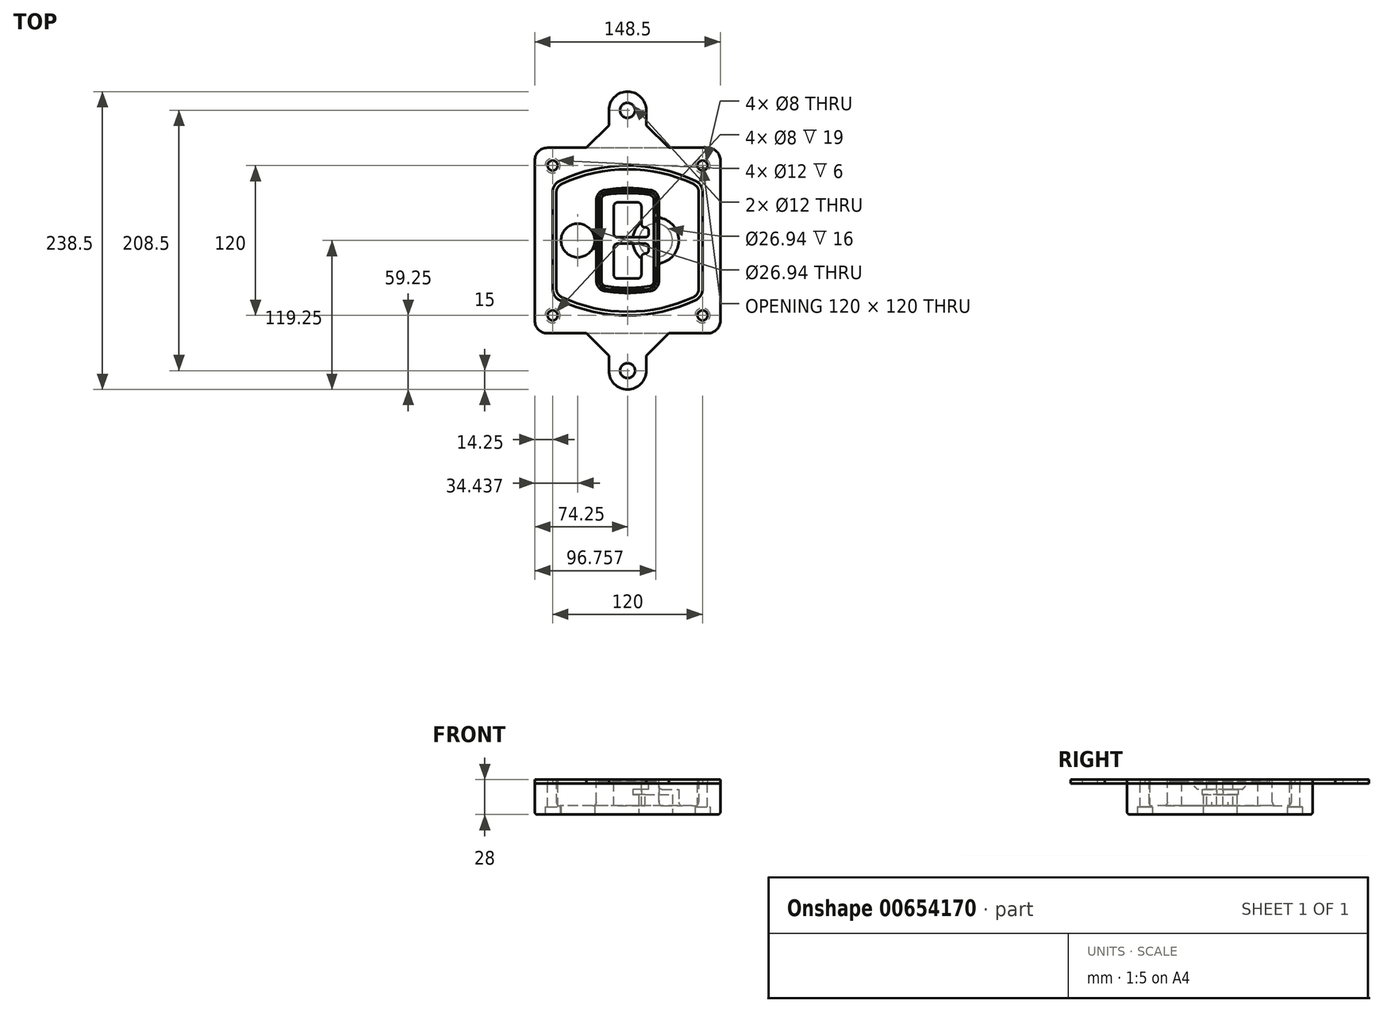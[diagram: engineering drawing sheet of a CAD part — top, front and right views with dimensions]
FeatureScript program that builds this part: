
annotation { "Feature Type Name" : "Feature", "Feature Type Description" : "" }
export const myFeature = defineFeature(function(context is Context, id is Id, definition is map)
    precondition{}
    {
        {
            var Q0;
            Q0=qCreatedBy(makeId("Top.planeOp"),FACE);
            var sketch = newSketch(context, id + "F0", { "sketchPlane" : qUnion([Q0])});
            skPoint(sketch, "E0.rect.middle", {"position": v(0, 0) * mm});
            skLineSegment(sketch, "E1.bottom", {"start": v(-64.25, -74.25) * mm, "end": v(64.25, -74.25) * mm});
            skLineSegment(sketch, "E1.top", {"start": v(-64.25, 74.25) * mm, "end": v(64.25, 74.25) * mm});
            skLineSegment(sketch, "E1.left", {"start": v(-74.25, -64.25) * mm, "end": v(-74.25, 64.25) * mm});
            skLineSegment(sketch, "E1.right", {"start": v(74.25, -64.25) * mm, "end": v(74.25, 64.25) * mm});
            skLineSegment(sketch, "E2", {"start": v(-74.25, 74.25) * mm, "end": v(74.25, -74.25) * mm, "construction": true});
            skLineSegment(sketch, "E3", {"start": v(74.25, 74.25) * mm, "end": v(-74.25, -74.25) * mm, "construction": true});
            skCircle(sketch, "E4", {"center": v(-60, 60) * mm, "radius": 4 * mm});
            skCircle(sketch, "E5", {"center": v(60, 60) * mm, "radius": 4 * mm});
            skCircle(sketch, "E6", {"center": v(60, -60) * mm, "radius": 4 * mm});
            skCircle(sketch, "E7", {"center": v(-60, -60) * mm, "radius": 4 * mm});
            skLineSegment(sketch, "E8", {"start": v(-60, 60) * mm, "end": v(60, 60) * mm, "construction": true});
            skLineSegment(sketch, "E9", {"start": v(60, 60) * mm, "end": v(60, -60) * mm, "construction": true});
            skLineSegment(sketch, "E10", {"start": v(60, -60) * mm, "end": v(-60, -60) * mm, "construction": true});
            skLineSegment(sketch, "E11", {"start": v(-60, -60) * mm, "end": v(-60, 60) * mm, "construction": true});
            skLineSegment(sketch, "E12", {"start": v(-60, 38.83) * mm, "end": v(-60, -38.83) * mm});
            skLineSegment(sketch, "E13", {"start": v(60, 38.83) * mm, "end": v(60, -38.83) * mm});
            skArc(sketch, "E14", {"start": v(54.26, 47.88) * mm, "mid": v(0, 60) * mm, "end": v(-54.26, 47.88) * mm});
            skArc(sketch, "E15", {"start": v(-54.26, -47.88) * mm, "mid": v(0, -60) * mm, "end": v(54.26, -47.88) * mm});
            skLineSegment(sketch, "E16", {"start": v(-60, 0) * mm, "end": v(60, 0) * mm, "construction": true});
            skPoint(sketch, "E17.visualSharp", {"position": v(-60, -45) * mm});
            skArc(sketch, "E17.filletArc", {"start": v(-60, -38.83) * mm, "mid": v(-58.44, -44.2) * mm, "end": v(-54.26, -47.88) * mm});
            skPoint(sketch, "E18.visualSharp", {"position": v(-60, 45) * mm});
            skArc(sketch, "E18.filletArc", {"start": v(-54.26, 47.88) * mm, "mid": v(-58.44, 44.2) * mm, "end": v(-60, 38.83) * mm});
            skPoint(sketch, "E19.visualSharp", {"position": v(60, 45) * mm});
            skArc(sketch, "E19.filletArc", {"start": v(60, 38.83) * mm, "mid": v(58.44, 44.2) * mm, "end": v(54.26, 47.88) * mm});
            skPoint(sketch, "E20.visualSharp", {"position": v(60, -45) * mm});
            skArc(sketch, "E20.filletArc", {"start": v(54.26, -47.88) * mm, "mid": v(58.44, -44.2) * mm, "end": v(60, -38.83) * mm});
            skPoint(sketch, "E21.visualSharp", {"position": v(-74.25, 74.25) * mm});
            skArc(sketch, "E21.filletArc", {"start": v(-64.25, 74.25) * mm, "mid": v(-71.32, 71.32) * mm, "end": v(-74.25, 64.25) * mm});
            skPoint(sketch, "E22.visualSharp", {"position": v(74.25, 74.25) * mm});
            skArc(sketch, "E22.filletArc", {"start": v(74.25, 64.25) * mm, "mid": v(71.32, 71.32) * mm, "end": v(64.25, 74.25) * mm});
            skPoint(sketch, "E23.visualSharp", {"position": v(74.25, -74.25) * mm});
            skArc(sketch, "E23.filletArc", {"start": v(64.25, -74.25) * mm, "mid": v(71.32, -71.32) * mm, "end": v(74.25, -64.25) * mm});
            skPoint(sketch, "E24.visualSharp", {"position": v(-74.25, -74.25) * mm});
            skArc(sketch, "E24.filletArc", {"start": v(-74.25, -64.25) * mm, "mid": v(-71.32, -71.32) * mm, "end": v(-64.25, -74.25) * mm});
            skArc(sketch, "E25.0", {"start": v(57, 38.83) * mm, "mid": v(55.9, 42.58) * mm, "end": v(52.98, 45.17) * mm});
            skLineSegment(sketch, "E25.1", {"start": v(57, 38.83) * mm, "end": v(57, -38.83) * mm});
            skArc(sketch, "E25.2", {"start": v(52.98, -45.17) * mm, "mid": v(55.9, -42.58) * mm, "end": v(57, -38.83) * mm});
            skArc(sketch, "E25.3", {"start": v(-52.98, -45.17) * mm, "mid": v(0, -57) * mm, "end": v(52.98, -45.17) * mm});
            skArc(sketch, "E25.4", {"start": v(-57, -38.83) * mm, "mid": v(-55.9, -42.58) * mm, "end": v(-52.98, -45.17) * mm});
            skArc(sketch, "E25.5", {"start": v(52.98, 45.17) * mm, "mid": v(0, 57) * mm, "end": v(-52.98, 45.17) * mm});
            skLineSegment(sketch, "E25.6", {"start": v(-57, 38.83) * mm, "end": v(-57, -38.83) * mm});
            skArc(sketch, "E25.7", {"start": v(-52.98, 45.17) * mm, "mid": v(-55.9, 42.58) * mm, "end": v(-57, 38.83) * mm});
            skArc(sketch, "E26.0", {"start": v(-55.96, 51.5) * mm, "mid": v(-61.82, 46.33) * mm, "end": v(-64, 38.83) * mm});
            skArc(sketch, "E26.1", {"start": v(55.96, 51.5) * mm, "mid": v(0, 64) * mm, "end": v(-55.96, 51.5) * mm});
            skArc(sketch, "E26.2", {"start": v(64, 38.83) * mm, "mid": v(61.82, 46.33) * mm, "end": v(55.96, 51.5) * mm});
            skLineSegment(sketch, "E26.3", {"start": v(64, 38.83) * mm, "end": v(64, -38.83) * mm});
            skArc(sketch, "E26.4", {"start": v(55.96, -51.5) * mm, "mid": v(61.82, -46.33) * mm, "end": v(64, -38.83) * mm});
            skLineSegment(sketch, "E26.5", {"start": v(-64, 38.83) * mm, "end": v(-64, -38.83) * mm});
            skArc(sketch, "E26.6", {"start": v(-55.96, -51.5) * mm, "mid": v(0, -64) * mm, "end": v(55.96, -51.5) * mm});
            skArc(sketch, "E26.7", {"start": v(-64, -38.83) * mm, "mid": v(-61.82, -46.33) * mm, "end": v(-55.96, -51.5) * mm});
            skLineSegment(sketch, "E27", {"start": v(0, 74.25) * mm, "end": v(0, 104.25) * mm, "construction": true});
            skCircle(sketch, "E28", {"center": v(0, 104.25) * mm, "radius": 6 * mm});
            skArc(sketch, "E29", {"start": v(-15, 104.25) * mm, "mid": v(0, 119.25) * mm, "end": v(15, 104.25) * mm});
            skLineSegment(sketch, "E30", {"start": v(-15, 104.25) * mm, "end": v(-15, 92.25) * mm});
            skLineSegment(sketch, "E31", {"start": v(15, 104.25) * mm, "end": v(15, 92.25) * mm});
            skLineSegment(sketch, "E32", {"start": v(-15, 92.25) * mm, "end": v(-33, 74.25) * mm});
            skLineSegment(sketch, "E33", {"start": v(15, 92.25) * mm, "end": v(33, 74.25) * mm});
            skLineSegment(sketch, "E34", {"start": v(0, -74.25) * mm, "end": v(0, -104.25) * mm, "construction": true});
            skCircle(sketch, "E35", {"center": v(0, -104.25) * mm, "radius": 6 * mm});
            skArc(sketch, "E36", {"start": v(15, -104.25) * mm, "mid": v(0, -119.25) * mm, "end": v(-15, -104.25) * mm});
            skLineSegment(sketch, "E37", {"start": v(15, -104.25) * mm, "end": v(15, -92.25) * mm});
            skLineSegment(sketch, "E38", {"start": v(-15, -104.25) * mm, "end": v(-15, -92.25) * mm});
            skLineSegment(sketch, "E39", {"start": v(15, -92.25) * mm, "end": v(33, -74.25) * mm});
            skLineSegment(sketch, "E40", {"start": v(-15, -92.25) * mm, "end": v(-33, -74.25) * mm});
            skSolve(sketch);
        }
        {
            var Q0;
            Q0=makeQuery(id+"F0.imprint","IMPRINT",FACE,{"disambiguationData":[TD([[makeQuery(id+"F0.imprint","IMPRINT",EDGE,{"derivedFrom":sQuery(id+"F0.wireOp",EDGE,"E1.bottom")}),1.0]])]});
            var Q1;
            Q1=makeQuery(id+"F0.imprint","IMPRINT",FACE,{"disambiguationData":[TD([[makeQuery(id+"F0.imprint","IMPRINT",EDGE,{"derivedFrom":sQuery(id+"F0.wireOp",EDGE,"E12")}),1.0]])]});
            var Q2;
            Q2=makeQuery(id+"F0.imprint","IMPRINT",FACE,{"disambiguationData":[TD([[makeQuery(id+"F0.imprint","IMPRINT",EDGE,{"derivedFrom":sQuery(id+"F0.wireOp",EDGE,"E25.0")}),1.0]])]});
            var Q3;
            Q3=makeQuery(id+"F0.imprint","IMPRINT",FACE,{"disambiguationData":[TD([[makeQuery(id+"F0.imprint","IMPRINT",EDGE,{"derivedFrom":sQuery(id+"F0.wireOp",EDGE,"E12")}),-1.0]])]});
            extrude(context, id + "F1", {"entities" : qUnion([Q0, Q1, Q2, Q3]), "oppositeDirection" : true, "depth" : 25 * mm});
        }
        {
            var Q0;
            Q0=makeQuery(id+"F0.imprint","IMPRINT",FACE,{"disambiguationData":[TD([[makeQuery(id+"F0.imprint","IMPRINT",EDGE,{"derivedFrom":sQuery(id+"F0.wireOp",EDGE,"E12")}),1.0]])]});
            extrude(context, id + "F2", {"entities" : qUnion([Q0]), "operationType" : NewBodyOperationType.ADD, "depth" : 3 * mm});
        }
        {
            var Q0;
            Q0=makeQuery(id+"F0.imprint","IMPRINT",FACE,{"disambiguationData":[TD([[makeQuery(id+"F0.imprint","IMPRINT",EDGE,{"derivedFrom":sQuery(id+"F0.wireOp",EDGE,"E25.0")}),1.0]])]});
            extrude(context, id + "F3", {"entities" : qUnion([Q0]), "operationType" : NewBodyOperationType.REMOVE, "oppositeDirection" : true, "depth" : 18 * mm});
        }
        {
            var Q0;
            Q0=makeQuery(id+"F2.opExtrude","CAP_FACE",FACE,{"disambiguationData":[OSD([sQuery(id+"F0.wireOp",EDGE,"E12"),sQuery(id+"F0.wireOp",EDGE,"E13"),sQuery(id+"F0.wireOp",EDGE,"E14"),sQuery(id+"F0.wireOp",EDGE,"E15"),sQuery(id+"F0.wireOp",EDGE,"E17.filletArc"),sQuery(id+"F0.wireOp",EDGE,"E18.filletArc"),sQuery(id+"F0.wireOp",EDGE,"E19.filletArc"),sQuery(id+"F0.wireOp",EDGE,"E20.filletArc"),sQuery(id+"F0.wireOp",EDGE,"E25.0"),sQuery(id+"F0.wireOp",EDGE,"E25.1"),sQuery(id+"F0.wireOp",EDGE,"E25.2"),sQuery(id+"F0.wireOp",EDGE,"E25.3"),sQuery(id+"F0.wireOp",EDGE,"E25.4"),sQuery(id+"F0.wireOp",EDGE,"E25.5"),sQuery(id+"F0.wireOp",EDGE,"E25.6"),sQuery(id+"F0.wireOp",EDGE,"E25.7")])],"isStart":false});
            var sketch = newSketch(context, id + "F4", { "sketchPlane" : qUnion([Q0])});
            skArc(sketch, "E41.0", {"start": v(-18.34, -40.45) * mm, "mid": v(0, -42) * mm, "end": v(18.34, -40.45) * mm});
            skArc(sketch, "E42.0", {"start": v(18.34, 40.45) * mm, "mid": v(0, 42) * mm, "end": v(-18.34, 40.45) * mm});
            skLineSegment(sketch, "E43", {"start": v(-25, 32.57) * mm, "end": v(-25, -32.57) * mm});
            skLineSegment(sketch, "E44", {"start": v(25, 32.57) * mm, "end": v(25, -32.57) * mm});
            skLineSegment(sketch, "E45", {"start": v(-25, 39.1) * mm, "end": v(25, 39.1) * mm, "construction": true});
            skLineSegment(sketch, "E46", {"start": v(-25, -39.1) * mm, "end": v(25, -39.1) * mm, "construction": true});
            skPoint(sketch, "E47.visualSharp", {"position": v(-25, 39.1) * mm});
            skArc(sketch, "E47.filletArc", {"start": v(-18.34, 40.45) * mm, "mid": v(-23.11, 37.73) * mm, "end": v(-25, 32.57) * mm});
            skPoint(sketch, "E48.visualSharp", {"position": v(25, 39.1) * mm});
            skArc(sketch, "E48.filletArc", {"start": v(25, 32.57) * mm, "mid": v(23.11, 37.73) * mm, "end": v(18.34, 40.45) * mm});
            skPoint(sketch, "E49.visualSharp", {"position": v(25, -39.1) * mm});
            skArc(sketch, "E49.filletArc", {"start": v(18.34, -40.45) * mm, "mid": v(23.11, -37.73) * mm, "end": v(25, -32.57) * mm});
            skPoint(sketch, "E50.visualSharp", {"position": v(-25, -39.1) * mm});
            skArc(sketch, "E50.filletArc", {"start": v(-25, -32.57) * mm, "mid": v(-23.11, -37.73) * mm, "end": v(-18.34, -40.45) * mm});
            skArc(sketch, "E51.0", {"start": v(52.98, 45.17) * mm, "mid": v(0, 57) * mm, "end": v(-52.98, 45.17) * mm});
            skArc(sketch, "E51.1", {"start": v(-52.98, 45.17) * mm, "mid": v(-55.9, 42.58) * mm, "end": v(-57, 38.83) * mm});
            skLineSegment(sketch, "E51.2", {"start": v(-57, 38.83) * mm, "end": v(-57, -38.83) * mm});
            skArc(sketch, "E51.3", {"start": v(-57, -38.83) * mm, "mid": v(-55.9, -42.58) * mm, "end": v(-52.98, -45.17) * mm});
            skArc(sketch, "E51.4", {"start": v(-52.98, -45.17) * mm, "mid": v(0, -57) * mm, "end": v(52.98, -45.17) * mm});
            skArc(sketch, "E51.5", {"start": v(52.98, -45.17) * mm, "mid": v(55.9, -42.58) * mm, "end": v(57, -38.83) * mm});
            skLineSegment(sketch, "E51.6", {"start": v(57, 38.83) * mm, "end": v(57, -38.83) * mm});
            skArc(sketch, "E51.7", {"start": v(57, 38.83) * mm, "mid": v(55.9, 42.58) * mm, "end": v(52.98, 45.17) * mm});
            skLineSegment(sketch, "E52.0", {"start": v(23, 32.57) * mm, "end": v(23, -32.57) * mm});
            skArc(sketch, "E52.1", {"start": v(18, -38.48) * mm, "mid": v(21.58, -36.44) * mm, "end": v(23, -32.57) * mm});
            skArc(sketch, "E52.2", {"start": v(-18, -38.48) * mm, "mid": v(0, -40) * mm, "end": v(18, -38.48) * mm});
            skArc(sketch, "E52.3", {"start": v(-23, -32.57) * mm, "mid": v(-21.58, -36.44) * mm, "end": v(-18, -38.48) * mm});
            skLineSegment(sketch, "E52.4", {"start": v(-23, 32.57) * mm, "end": v(-23, -32.57) * mm});
            skArc(sketch, "E52.5", {"start": v(23, 32.57) * mm, "mid": v(21.58, 36.44) * mm, "end": v(18, 38.48) * mm});
            skArc(sketch, "E52.6", {"start": v(-18, 38.48) * mm, "mid": v(-21.58, 36.44) * mm, "end": v(-23, 32.57) * mm});
            skArc(sketch, "E52.7", {"start": v(18, 38.48) * mm, "mid": v(0, 40) * mm, "end": v(-18, 38.48) * mm});
            skArc(sketch, "E53.0", {"start": v(21, 32.57) * mm, "mid": v(20.06, 35.15) * mm, "end": v(17.67, 36.5) * mm});
            skLineSegment(sketch, "E53.1", {"start": v(21, 32.57) * mm, "end": v(21, -32.57) * mm});
            skArc(sketch, "E53.2", {"start": v(17.67, -36.5) * mm, "mid": v(20.06, -35.15) * mm, "end": v(21, -32.57) * mm});
            skArc(sketch, "E53.3", {"start": v(-17.67, -36.5) * mm, "mid": v(0, -38) * mm, "end": v(17.67, -36.5) * mm});
            skArc(sketch, "E53.4", {"start": v(-21, -32.57) * mm, "mid": v(-20.06, -35.15) * mm, "end": v(-17.67, -36.5) * mm});
            skArc(sketch, "E53.5", {"start": v(17.67, 36.5) * mm, "mid": v(0, 38) * mm, "end": v(-17.67, 36.5) * mm});
            skLineSegment(sketch, "E53.6", {"start": v(-21, 32.57) * mm, "end": v(-21, -32.57) * mm});
            skArc(sketch, "E53.7", {"start": v(-17.67, 36.5) * mm, "mid": v(-20.06, 35.15) * mm, "end": v(-21, 32.57) * mm});
            skLineSegment(sketch, "E54", {"start": v(-25, 0) * mm, "end": v(25, 0) * mm, "construction": true});
            skLineSegment(sketch, "E55", {"start": v(-11, 5.5) * mm, "end": v(-11, 27.5) * mm});
            skLineSegment(sketch, "E56", {"start": v(-8, 30.5) * mm, "end": v(8, 30.5) * mm});
            skLineSegment(sketch, "E57", {"start": v(11, 27.5) * mm, "end": v(11, 13.5) * mm});
            skLineSegment(sketch, "E58", {"start": v(14, 10.5) * mm, "end": v(14, 10.5) * mm});
            skLineSegment(sketch, "E59", {"start": v(17, 7.5) * mm, "end": v(17, 5.5) * mm});
            skLineSegment(sketch, "E60", {"start": v(14, 2.5) * mm, "end": v(-8, 2.5) * mm});
            skPoint(sketch, "E61.visualSharp", {"position": v(-11, 30.5) * mm});
            skArc(sketch, "E61.filletArc", {"start": v(-8, 30.5) * mm, "mid": v(-10.12, 29.62) * mm, "end": v(-11, 27.5) * mm});
            skPoint(sketch, "E62.visualSharp", {"position": v(11, 30.5) * mm});
            skArc(sketch, "E62.filletArc", {"start": v(11, 27.5) * mm, "mid": v(10.12, 29.62) * mm, "end": v(8, 30.5) * mm});
            skPoint(sketch, "E63.visualSharp", {"position": v(11, 10.5) * mm});
            skArc(sketch, "E63.filletArc", {"start": v(11, 13.5) * mm, "mid": v(11.88, 11.38) * mm, "end": v(14, 10.5) * mm});
            skPoint(sketch, "E64.visualSharp", {"position": v(17, 10.5) * mm});
            skArc(sketch, "E64.filletArc", {"start": v(17, 7.5) * mm, "mid": v(16.12, 9.62) * mm, "end": v(14, 10.5) * mm});
            skPoint(sketch, "E65.visualSharp", {"position": v(17, 2.5) * mm});
            skArc(sketch, "E65.filletArc", {"start": v(14, 2.5) * mm, "mid": v(16.12, 3.38) * mm, "end": v(17, 5.5) * mm});
            skPoint(sketch, "E66.visualSharp", {"position": v(-11, 2.5) * mm});
            skArc(sketch, "E66.filletArc", {"start": v(-11, 5.5) * mm, "mid": v(-10.12, 3.38) * mm, "end": v(-8, 2.5) * mm});
            skLineSegment(sketch, "E67.0.MirrorCS", {"start": v(14, -2.5) * mm, "end": v(-8, -2.5) * mm});
            skArc(sketch, "E68.0.MirrorCS", {"start": v(-11, -5.5) * mm, "mid": v(-10.12, -3.38) * mm, "end": v(-8, -2.5) * mm});
            skLineSegment(sketch, "E69.0.MirrorCS", {"start": v(-11, -5.5) * mm, "end": v(-11, -27.5) * mm});
            skArc(sketch, "E70.0.MirrorCS", {"start": v(-8, -30.5) * mm, "mid": v(-10.12, -29.62) * mm, "end": v(-11, -27.5) * mm});
            skLineSegment(sketch, "E71.0.MirrorCS", {"start": v(-8, -30.5) * mm, "end": v(8, -30.5) * mm});
            skArc(sketch, "E72.0.MirrorCS", {"start": v(11, -27.5) * mm, "mid": v(10.12, -29.62) * mm, "end": v(8, -30.5) * mm});
            skLineSegment(sketch, "E73.0.MirrorCS", {"start": v(11, -27.5) * mm, "end": v(11, -13.5) * mm});
            skArc(sketch, "E74.0.MirrorCS", {"start": v(11, -13.5) * mm, "mid": v(11.88, -11.38) * mm, "end": v(14, -10.5) * mm});
            skArc(sketch, "E75.0.MirrorCS", {"start": v(17, -7.5) * mm, "mid": v(16.12, -9.62) * mm, "end": v(14, -10.5) * mm});
            skLineSegment(sketch, "E76.0.MirrorCS", {"start": v(17, -7.5) * mm, "end": v(17, -5.5) * mm});
            skArc(sketch, "E77.0.MirrorCS", {"start": v(14, -2.5) * mm, "mid": v(16.12, -3.38) * mm, "end": v(17, -5.5) * mm});
            skSolve(sketch);
        }
        {
            var Q0;
            Q0=makeQuery(id+"F4.imprint","IMPRINT",FACE,{"disambiguationData":[TD([[makeQuery(id+"F4.imprint","IMPRINT",EDGE,{"derivedFrom":sQuery(id+"F4.wireOp",EDGE,"E41.0")}),1.0]])]});
            var Q1;
            Q1=makeQuery(id+"F4.imprint","IMPRINT",FACE,{"disambiguationData":[TD([[makeQuery(id+"F4.imprint","IMPRINT",EDGE,{"derivedFrom":sQuery(id+"F4.wireOp",EDGE,"E52.0")}),-1.0]])]});
            var Q2;
            Q2=makeQuery(id+"F4.imprint","IMPRINT",FACE,{"disambiguationData":[TD([[makeQuery(id+"F4.imprint","IMPRINT",EDGE,{"derivedFrom":sQuery(id+"F4.wireOp",EDGE,"E53.0")}),1.0]])]});
            extrude(context, id + "F5", {"entities" : qUnion([Q0, Q1, Q2]), "operationType" : NewBodyOperationType.ADD, "endBound" : BoundingType.UP_TO_NEXT, "oppositeDirection" : true, "depth" : 25 * mm});
        }
        {
            var Q0;
            Q0=makeQuery(id+"F4.imprint","IMPRINT",FACE,{"disambiguationData":[TD([[makeQuery(id+"F4.imprint","IMPRINT",EDGE,{"derivedFrom":sQuery(id+"F4.wireOp",EDGE,"E52.0")}),-1.0]])]});
            extrude(context, id + "F6", {"entities" : qUnion([Q0]), "operationType" : NewBodyOperationType.REMOVE, "oppositeDirection" : true, "depth" : 2 * mm});
        }
        {
            var Q0;
            Q0=makeQuery(id+"F1.opExtrude","CAP_FACE",FACE,{"disambiguationData":[OSD([sQuery(id+"F0.wireOp",EDGE,"E1.bottom"),sQuery(id+"F0.wireOp",EDGE,"E1.top"),sQuery(id+"F0.wireOp",EDGE,"E1.left"),sQuery(id+"F0.wireOp",EDGE,"E1.right"),sQuery(id+"F0.wireOp",EDGE,"E4"),sQuery(id+"F0.wireOp",EDGE,"E5"),sQuery(id+"F0.wireOp",EDGE,"E6"),sQuery(id+"F0.wireOp",EDGE,"E7"),sQuery(id+"F0.wireOp",EDGE,"E21.filletArc"),sQuery(id+"F0.wireOp",EDGE,"E22.filletArc"),sQuery(id+"F0.wireOp",EDGE,"E23.filletArc"),sQuery(id+"F0.wireOp",EDGE,"E24.filletArc")])],"isStart":false});
            var sketch = newSketch(context, id + "F7", { "sketchPlane" : qUnion([Q0])});
            skCircle(sketch, "E78", {"center": v(22.5, 0) * mm, "radius": 13.47 * mm});
            skCircle(sketch, "E79", {"center": v(-39.81, 0) * mm, "radius": 13.47 * mm});
            skLineSegment(sketch, "E80", {"start": v(74.25, 0) * mm, "end": v(-74.25, 0) * mm});
            skCircle(sketch, "E81", {"center": v(22.5, 0) * mm, "radius": 18.47 * mm});
            skCircle(sketch, "E82", {"center": v(60, -60) * mm, "radius": 6 * mm});
            skCircle(sketch, "E83", {"center": v(-60, -60) * mm, "radius": 6 * mm});
            skCircle(sketch, "E84", {"center": v(-60, 60) * mm, "radius": 6 * mm});
            skCircle(sketch, "E85", {"center": v(60, 60) * mm, "radius": 6 * mm});
            skSolve(sketch);
        }
        {
            var Q0;
            {var subQ1=sQuery(id+"F7.wireOp",EDGE,"E80");var subQ4=sQuery(id+"F7.wireOp",EDGE,"E78");var subQ6=makeQuery(id+"F7.imprint","INTERSECT",VERTEX,{"disambiguationData":[OD(0.0)],"derivedFrom":[subQ4,subQ1]});Q0=makeQuery(id+"F7.imprint","IMPRINT",FACE,{"disambiguationData":[TD([[makeQuery(id+"F7.imprint","IMPRINT",EDGE,{"disambiguationData":[TD([[subQ6,-1.0]])],"derivedFrom":subQ4}),-1.0]])]});}
            var Q1;
            {var subQ0=sQuery(id+"F7.wireOp",EDGE,"E80");var subQ1=sQuery(id+"F7.wireOp",EDGE,"E78");var subQ3=makeQuery(id+"F7.imprint","INTERSECT",VERTEX,{"disambiguationData":[OD(0.0)],"derivedFrom":[subQ1,subQ0]});Q1=makeQuery(id+"F7.imprint","IMPRINT",FACE,{"disambiguationData":[TD([[makeQuery(id+"F7.imprint","IMPRINT",EDGE,{"disambiguationData":[TD([[subQ3,-1.0]])],"derivedFrom":subQ1}),1.0]])]});}
            var Q2;
            {var subQ0=sQuery(id+"F7.wireOp",EDGE,"E80");var subQ1=sQuery(id+"F7.wireOp",EDGE,"E78");var subQ3=makeQuery(id+"F7.imprint","INTERSECT",VERTEX,{"disambiguationData":[OD(0.0)],"derivedFrom":[subQ1,subQ0]});Q2=makeQuery(id+"F7.imprint","IMPRINT",FACE,{"disambiguationData":[TD([[makeQuery(id+"F7.imprint","IMPRINT",EDGE,{"disambiguationData":[TD([[subQ3,1.0]])],"derivedFrom":subQ1}),1.0]])]});}
            var Q3;
            {var subQ1=sQuery(id+"F7.wireOp",EDGE,"E80");var subQ4=sQuery(id+"F7.wireOp",EDGE,"E78");var subQ6=makeQuery(id+"F7.imprint","INTERSECT",VERTEX,{"disambiguationData":[OD(0.0)],"derivedFrom":[subQ4,subQ1]});Q3=makeQuery(id+"F7.imprint","IMPRINT",FACE,{"disambiguationData":[TD([[makeQuery(id+"F7.imprint","IMPRINT",EDGE,{"disambiguationData":[TD([[subQ6,1.0]])],"derivedFrom":subQ4}),-1.0]])]});}
            extrude(context, id + "F8", {"entities" : qUnion([Q0, Q1, Q2, Q3]), "operationType" : NewBodyOperationType.ADD, "oppositeDirection" : true, "depth" : 20 * mm});
        }
        {
            var Q0;
            {var subQ0=sQuery(id+"F7.wireOp",EDGE,"E80");var subQ1=sQuery(id+"F7.wireOp",EDGE,"E78");var subQ3=makeQuery(id+"F7.imprint","INTERSECT",VERTEX,{"disambiguationData":[OD(0.0)],"derivedFrom":[subQ1,subQ0]});Q0=makeQuery(id+"F7.imprint","IMPRINT",FACE,{"disambiguationData":[TD([[makeQuery(id+"F7.imprint","IMPRINT",EDGE,{"disambiguationData":[TD([[subQ3,-1.0]])],"derivedFrom":subQ1}),1.0]])]});}
            var Q1;
            {var subQ0=sQuery(id+"F7.wireOp",EDGE,"E80");var subQ1=sQuery(id+"F7.wireOp",EDGE,"E78");var subQ3=makeQuery(id+"F7.imprint","INTERSECT",VERTEX,{"disambiguationData":[OD(0.0)],"derivedFrom":[subQ1,subQ0]});Q1=makeQuery(id+"F7.imprint","IMPRINT",FACE,{"disambiguationData":[TD([[makeQuery(id+"F7.imprint","IMPRINT",EDGE,{"disambiguationData":[TD([[subQ3,1.0]])],"derivedFrom":subQ1}),1.0]])]});}
            extrude(context, id + "F9", {"entities" : qUnion([Q0, Q1]), "operationType" : NewBodyOperationType.REMOVE, "oppositeDirection" : true, "depth" : 16 * mm});
        }
        {
            var Q0;
            {var subQ0=sQuery(id+"F7.wireOp",EDGE,"E80");var subQ1=sQuery(id+"F7.wireOp",EDGE,"E79");var subQ3=makeQuery(id+"F7.imprint","INTERSECT",VERTEX,{"disambiguationData":[OD(0.0)],"derivedFrom":[subQ1,subQ0]});Q0=makeQuery(id+"F7.imprint","IMPRINT",FACE,{"disambiguationData":[TD([[makeQuery(id+"F7.imprint","IMPRINT",EDGE,{"disambiguationData":[TD([[subQ3,-1.0]])],"derivedFrom":subQ1}),1.0]])]});}
            var Q1;
            {var subQ0=sQuery(id+"F7.wireOp",EDGE,"E80");var subQ1=sQuery(id+"F7.wireOp",EDGE,"E79");var subQ3=makeQuery(id+"F7.imprint","INTERSECT",VERTEX,{"disambiguationData":[OD(0.0)],"derivedFrom":[subQ1,subQ0]});Q1=makeQuery(id+"F7.imprint","IMPRINT",FACE,{"disambiguationData":[TD([[makeQuery(id+"F7.imprint","IMPRINT",EDGE,{"disambiguationData":[TD([[subQ3,1.0]])],"derivedFrom":subQ1}),1.0]])]});}
            extrude(context, id + "F10", {"entities" : qUnion([Q0, Q1]), "operationType" : NewBodyOperationType.REMOVE, "oppositeDirection" : true, "depth" : 25 * mm});
        }
        {
            var Q0;
            Q0=makeQuery(id+"F7.imprint","IMPRINT",FACE,{"disambiguationData":[TD([[makeQuery(id+"F7.imprint","IMPRINT",EDGE,{"derivedFrom":sQuery(id+"F7.wireOp",EDGE,"E82")}),1.0]])]});
            var Q1;
            Q1=makeQuery(id+"F7.imprint","IMPRINT",FACE,{"disambiguationData":[TD([[makeQuery(id+"F7.imprint","IMPRINT",EDGE,{"derivedFrom":makeQuery(id+"F1.opExtrude","CAP_EDGE",EDGE,{"disambiguationData":[OSD([sQuery(id+"F0.wireOp",EDGE,"E5")])],"isStart":false})}),-1.0]])]});
            var Q2;
            Q2=makeQuery(id+"F7.imprint","IMPRINT",FACE,{"disambiguationData":[TD([[makeQuery(id+"F7.imprint","IMPRINT",EDGE,{"derivedFrom":sQuery(id+"F7.wireOp",EDGE,"E83")}),1.0]])]});
            var Q3;
            Q3=makeQuery(id+"F7.imprint","IMPRINT",FACE,{"disambiguationData":[TD([[makeQuery(id+"F7.imprint","IMPRINT",EDGE,{"derivedFrom":makeQuery(id+"F1.opExtrude","CAP_EDGE",EDGE,{"disambiguationData":[OSD([sQuery(id+"F0.wireOp",EDGE,"E4")])],"isStart":false})}),-1.0]])]});
            var Q4;
            Q4=makeQuery(id+"F7.imprint","IMPRINT",FACE,{"disambiguationData":[TD([[makeQuery(id+"F7.imprint","IMPRINT",EDGE,{"derivedFrom":sQuery(id+"F7.wireOp",EDGE,"E84")}),1.0]])]});
            var Q5;
            Q5=makeQuery(id+"F7.imprint","IMPRINT",FACE,{"disambiguationData":[TD([[makeQuery(id+"F7.imprint","IMPRINT",EDGE,{"derivedFrom":makeQuery(id+"F1.opExtrude","CAP_EDGE",EDGE,{"disambiguationData":[OSD([sQuery(id+"F0.wireOp",EDGE,"E7")])],"isStart":false})}),-1.0]])]});
            var Q6;
            Q6=makeQuery(id+"F7.imprint","IMPRINT",FACE,{"disambiguationData":[TD([[makeQuery(id+"F7.imprint","IMPRINT",EDGE,{"derivedFrom":sQuery(id+"F7.wireOp",EDGE,"E85")}),1.0]])]});
            var Q7;
            Q7=makeQuery(id+"F7.imprint","IMPRINT",FACE,{"disambiguationData":[TD([[makeQuery(id+"F7.imprint","IMPRINT",EDGE,{"derivedFrom":makeQuery(id+"F1.opExtrude","CAP_EDGE",EDGE,{"disambiguationData":[OSD([sQuery(id+"F0.wireOp",EDGE,"E6")])],"isStart":false})}),-1.0]])]});
            extrude(context, id + "F11", {"entities" : qUnion([Q0, Q1, Q2, Q3, Q4, Q5, Q6, Q7]), "operationType" : NewBodyOperationType.REMOVE, "oppositeDirection" : true, "depth" : 6 * mm});
        }
        {
            var Q0;
            Q0=makeQuery(id+"F9.boolean.opBoolean","COPY",FACE,{"derivedFrom":makeQuery(id+"F9.opExtrude","CAP_FACE",FACE,{"disambiguationData":[OSD([sQuery(id+"F7.wireOp",EDGE,"E78")])],"isStart":false})});
            var sketch = newSketch(context, id + "F12", { "sketchPlane" : qUnion([Q0])});
            skArc(sketch, "E86.0", {"start": v(11, 14.45) * mm, "mid": v(6.45, 9.13) * mm, "end": v(4.2, 2.5) * mm});
            skArc(sketch, "E86.1", {"start": v(4.2, -2.5) * mm, "mid": v(6.45, -9.13) * mm, "end": v(11, -14.45) * mm});
            skLineSegment(sketch, "E87", {"start": v(4.2, -2.5) * mm, "end": v(14, -2.5) * mm});
            skLineSegment(sketch, "E88.0", {"start": v(14, 2.5) * mm, "end": v(4.2, 2.5) * mm});
            skArc(sketch, "E88.1", {"start": v(14, 2.5) * mm, "mid": v(16.12, 3.38) * mm, "end": v(17, 5.5) * mm});
            skLineSegment(sketch, "E88.2", {"start": v(17, 7.5) * mm, "end": v(17, 5.5) * mm});
            skArc(sketch, "E88.3", {"start": v(17, 7.5) * mm, "mid": v(16.12, 9.62) * mm, "end": v(14, 10.5) * mm});
            skArc(sketch, "E88.4", {"start": v(11, 13.5) * mm, "mid": v(11.88, 11.38) * mm, "end": v(14, 10.5) * mm});
            skLineSegment(sketch, "E88.5", {"start": v(11, 14.45) * mm, "end": v(11, 13.5) * mm});
            skLineSegment(sketch, "E88.7", {"start": v(14, -2.5) * mm, "end": v(4.2, -2.5) * mm});
            skArc(sketch, "E88.8", {"start": v(14, -2.5) * mm, "mid": v(16.12, -3.38) * mm, "end": v(17, -5.5) * mm});
            skLineSegment(sketch, "E88.9", {"start": v(17, -7.5) * mm, "end": v(17, -5.5) * mm});
            skArc(sketch, "E88.10", {"start": v(17, -7.5) * mm, "mid": v(16.12, -9.62) * mm, "end": v(14, -10.5) * mm});
            skArc(sketch, "E88.11", {"start": v(11, -13.5) * mm, "mid": v(11.88, -11.38) * mm, "end": v(14, -10.5) * mm});
            skLineSegment(sketch, "E88.12", {"start": v(11, -14.45) * mm, "end": v(11, -13.5) * mm});
            skPoint(sketch, "E89.orphan", {"position": v(11, -27.5) * mm});
            skPoint(sketch, "E90.orphan", {"position": v(-8, -2.5) * mm});
            skPoint(sketch, "E91.orphan", {"position": v(-8, 2.5) * mm});
            skPoint(sketch, "E92.orphan", {"position": v(11, 27.5) * mm});
            skSolve(sketch);
        }
        {
            var Q0;
            {var subQ7=sQuery(id+"F12.wireOp",EDGE,"E86.0");var subQ14=sQuery(id+"F12.wireOp",EDGE,"E86.1");var subQ16=sQuery(id+"F12.wireOp",EDGE,"E88.1");var subQ18=sQuery(id+"F12.wireOp",EDGE,"E88.8");Q0=qUnion([makeQuery(id+"F12.imprint","IMPRINT",FACE,{"disambiguationData":[TD([[makeQuery(id+"F12.imprint","IMPRINT",EDGE,{"derivedFrom":subQ7}),1.0]])]}),makeQuery(id+"F12.imprint","IMPRINT",FACE,{"disambiguationData":[TD([[makeQuery(id+"F12.imprint","IMPRINT",EDGE,{"derivedFrom":subQ14}),1.0]])]}),makeQuery(id+"F12.imprint","IMPRINT",FACE,{"disambiguationData":[TD([[makeQuery(id+"F12.imprint","IMPRINT",EDGE,{"derivedFrom":subQ16}),1.0]])]}),makeQuery(id+"F12.imprint","IMPRINT",FACE,{"disambiguationData":[TD([[makeQuery(id+"F12.imprint","IMPRINT",EDGE,{"derivedFrom":subQ18}),-1.0]])]})]);}
            var Q1;
            Q1=makeQuery(id+"F5.boolean.opBoolean","SPLIT",FACE,{"disambiguationData":[TD([makeQuery(id+"F5.opExtrude","SWEPT_FACE",FACE,{"disambiguationData":[OSD([sQuery(id+"F4.wireOp",EDGE,"E55")])]})])],"derivedFrom":makeQuery(id+"F3.boolean.opBoolean","COPY",FACE,{"derivedFrom":makeQuery(id+"F3.opExtrude","CAP_FACE",FACE,{"disambiguationData":[OSD([sQuery(id+"F0.wireOp",EDGE,"E25.0"),sQuery(id+"F0.wireOp",EDGE,"E25.1"),sQuery(id+"F0.wireOp",EDGE,"E25.2"),sQuery(id+"F0.wireOp",EDGE,"E25.3"),sQuery(id+"F0.wireOp",EDGE,"E25.4"),sQuery(id+"F0.wireOp",EDGE,"E25.5"),sQuery(id+"F0.wireOp",EDGE,"E25.6"),sQuery(id+"F0.wireOp",EDGE,"E25.7")])],"isStart":false})})});
            extrude(context, id + "F13", {"entities" : qUnion([Q0]), "operationType" : NewBodyOperationType.REMOVE, "endBound" : BoundingType.UP_TO_SURFACE, "endBoundEntityFace" : qUnion([Q1]), "depth" : 25 * mm});
        }
        {
            var Q0;
            Q0=makeQuery(id+"F3.boolean.opBoolean","COPY",EDGE,{"derivedFrom":makeQuery(id+"F3.opExtrude","CAP_EDGE",EDGE,{"disambiguationData":[OSD([sQuery(id+"F0.wireOp",EDGE,"E25.6")])],"isStart":false})});
            var Q1;
            Q1=makeQuery(id+"F8.boolean.opBoolean","INTERSECT",EDGE,{"derivedFrom":[makeQuery(id+"F5.opExtrude","SWEPT_FACE",FACE,{"disambiguationData":[OSD([sQuery(id+"F4.wireOp",EDGE,"E44")])]}),makeQuery(id+"F8.opExtrude","CAP_FACE",FACE,{"disambiguationData":[OSD([sQuery(id+"F7.wireOp",EDGE,"E81")])],"isStart":false})]});
            var Q2;
            Q2=makeQuery(id+"F8.boolean.opBoolean","INTERSECT",EDGE,{"disambiguationData":[OD(1.0)],"derivedFrom":[makeQuery(id+"F5.opExtrude","SWEPT_FACE",FACE,{"disambiguationData":[OSD([sQuery(id+"F4.wireOp",EDGE,"E44")])]}),makeQuery(id+"F8.opExtrude","SWEPT_FACE",FACE,{"disambiguationData":[OSD([sQuery(id+"F7.wireOp",EDGE,"E81")])]})]});
            var Q3;
            {var subQ0=sQuery(id+"F4.wireOp",EDGE,"E44");Q3=makeQuery(id+"F8.boolean.opBoolean","SPLIT",EDGE,{"disambiguationData":[TD([makeQuery(id+"F5.opExtrude","SWEPT_FACE",FACE,{"disambiguationData":[OSD([sQuery(id+"F4.wireOp",EDGE,"E49.filletArc")])]})])],"derivedFrom":makeQuery(id+"F5.opExtrude","CAP_EDGE",EDGE,{"disambiguationData":[OSD([subQ0])],"isStart":false})});}
            var Q4;
            {var subQ0=sQuery(id+"F0.wireOp",EDGE,"E25.7");var subQ1=sQuery(id+"F0.wireOp",EDGE,"E25.1");var subQ2=sQuery(id+"F0.wireOp",EDGE,"E25.6");var subQ3=sQuery(id+"F0.wireOp",EDGE,"E25.5");var subQ4=sQuery(id+"F0.wireOp",EDGE,"E25.4");var subQ5=sQuery(id+"F0.wireOp",EDGE,"E25.0");var subQ6=sQuery(id+"F0.wireOp",EDGE,"E25.2");var subQ7=sQuery(id+"F0.wireOp",EDGE,"E25.3");Q4=makeQuery(id+"F8.boolean.opBoolean","INTERSECT",EDGE,{"derivedFrom":[makeQuery(id+"F5.boolean.opBoolean","SPLIT",FACE,{"disambiguationData":[TD([makeQuery(id+"F2.opExtrude","SWEPT_FACE",FACE,{"disambiguationData":[OSD([subQ5])]})])],"derivedFrom":makeQuery(id+"F3.boolean.opBoolean","COPY",FACE,{"derivedFrom":makeQuery(id+"F3.opExtrude","CAP_FACE",FACE,{"disambiguationData":[OSD([subQ5,subQ1,subQ6,subQ7,subQ4,subQ3,subQ2,subQ0])],"isStart":false})})}),makeQuery(id+"F8.opExtrude","SWEPT_FACE",FACE,{"disambiguationData":[OSD([sQuery(id+"F7.wireOp",EDGE,"E81")])]})]});}
            var Q5;
            Q5=makeQuery(id+"F8.boolean.opBoolean","INTERSECT",EDGE,{"disambiguationData":[OD(0.0)],"derivedFrom":[makeQuery(id+"F5.opExtrude","SWEPT_FACE",FACE,{"disambiguationData":[OSD([sQuery(id+"F4.wireOp",EDGE,"E44")])]}),makeQuery(id+"F8.opExtrude","SWEPT_FACE",FACE,{"disambiguationData":[OSD([sQuery(id+"F7.wireOp",EDGE,"E81")])]})]});
            fillet(context, id + "F14", {"entities" : qUnion([Q0, Q1, Q2, Q3, Q4, Q5]), "radius" : 3 * mm, "tangentPropagation" : true, "allowEdgeOverflow" : false});
        }
        {
            var Q0;
            Q0=makeQuery(id+"F1.opExtrude","CAP_EDGE",EDGE,{"disambiguationData":[OSD([sQuery(id+"F0.wireOp",EDGE,"E1.bottom")])],"isStart":false});
            fillet(context, id + "F15", {"entities" : qUnion([Q0]), "radius" : 2 * mm, "tangentPropagation" : true, "allowEdgeOverflow" : false});
        }
        {
            var Q0;
            Q0=makeQuery(id+"F0.imprint","IMPRINT",FACE,{"disambiguationData":[TD([[makeQuery(id+"F0.imprint","IMPRINT",EDGE,{"derivedFrom":sQuery(id+"F0.wireOp",EDGE,"E35")}),-1.0]])]});
            var Q1;
            Q1=makeQuery(id+"F0.imprint","IMPRINT",FACE,{"disambiguationData":[TD([[makeQuery(id+"F0.imprint","IMPRINT",EDGE,{"derivedFrom":sQuery(id+"F0.wireOp",EDGE,"E1.left")}),-1.0]])]});
            var Q2;
            Q2=makeQuery(id+"F0.imprint","IMPRINT",FACE,{"disambiguationData":[TD([[makeQuery(id+"F0.imprint","IMPRINT",EDGE,{"derivedFrom":sQuery(id+"F0.wireOp",EDGE,"E28")}),-1.0]])]});
            var Q3;
            Q3=makeQuery(id+"F0.imprint","IMPRINT",FACE,{"disambiguationData":[TD([[makeQuery(id+"F0.imprint","IMPRINT",EDGE,{"derivedFrom":sQuery(id+"F0.wireOp",EDGE,"E12")}),-1.0]])]});
            var Q4;
            Q4=makeQuery(id+"F2.opExtrude","CAP_FACE",FACE,{"disambiguationData":[OSD([sQuery(id+"F0.wireOp",EDGE,"E12"),sQuery(id+"F0.wireOp",EDGE,"E13"),sQuery(id+"F0.wireOp",EDGE,"E14"),sQuery(id+"F0.wireOp",EDGE,"E15"),sQuery(id+"F0.wireOp",EDGE,"E17.filletArc"),sQuery(id+"F0.wireOp",EDGE,"E18.filletArc"),sQuery(id+"F0.wireOp",EDGE,"E19.filletArc"),sQuery(id+"F0.wireOp",EDGE,"E20.filletArc"),sQuery(id+"F0.wireOp",EDGE,"E25.0"),sQuery(id+"F0.wireOp",EDGE,"E25.1"),sQuery(id+"F0.wireOp",EDGE,"E25.2"),sQuery(id+"F0.wireOp",EDGE,"E25.3"),sQuery(id+"F0.wireOp",EDGE,"E25.4"),sQuery(id+"F0.wireOp",EDGE,"E25.5"),sQuery(id+"F0.wireOp",EDGE,"E25.6"),sQuery(id+"F0.wireOp",EDGE,"E25.7")])],"isStart":false});
            extrude(context, id + "F16", {"entities" : qUnion([Q0, Q1, Q2, Q3]), "endBound" : BoundingType.UP_TO_SURFACE, "depth" : 25 * mm, "endBoundEntityFace" : qUnion([Q4]), "offsetDistance" : 25 * mm});
        }
    });
